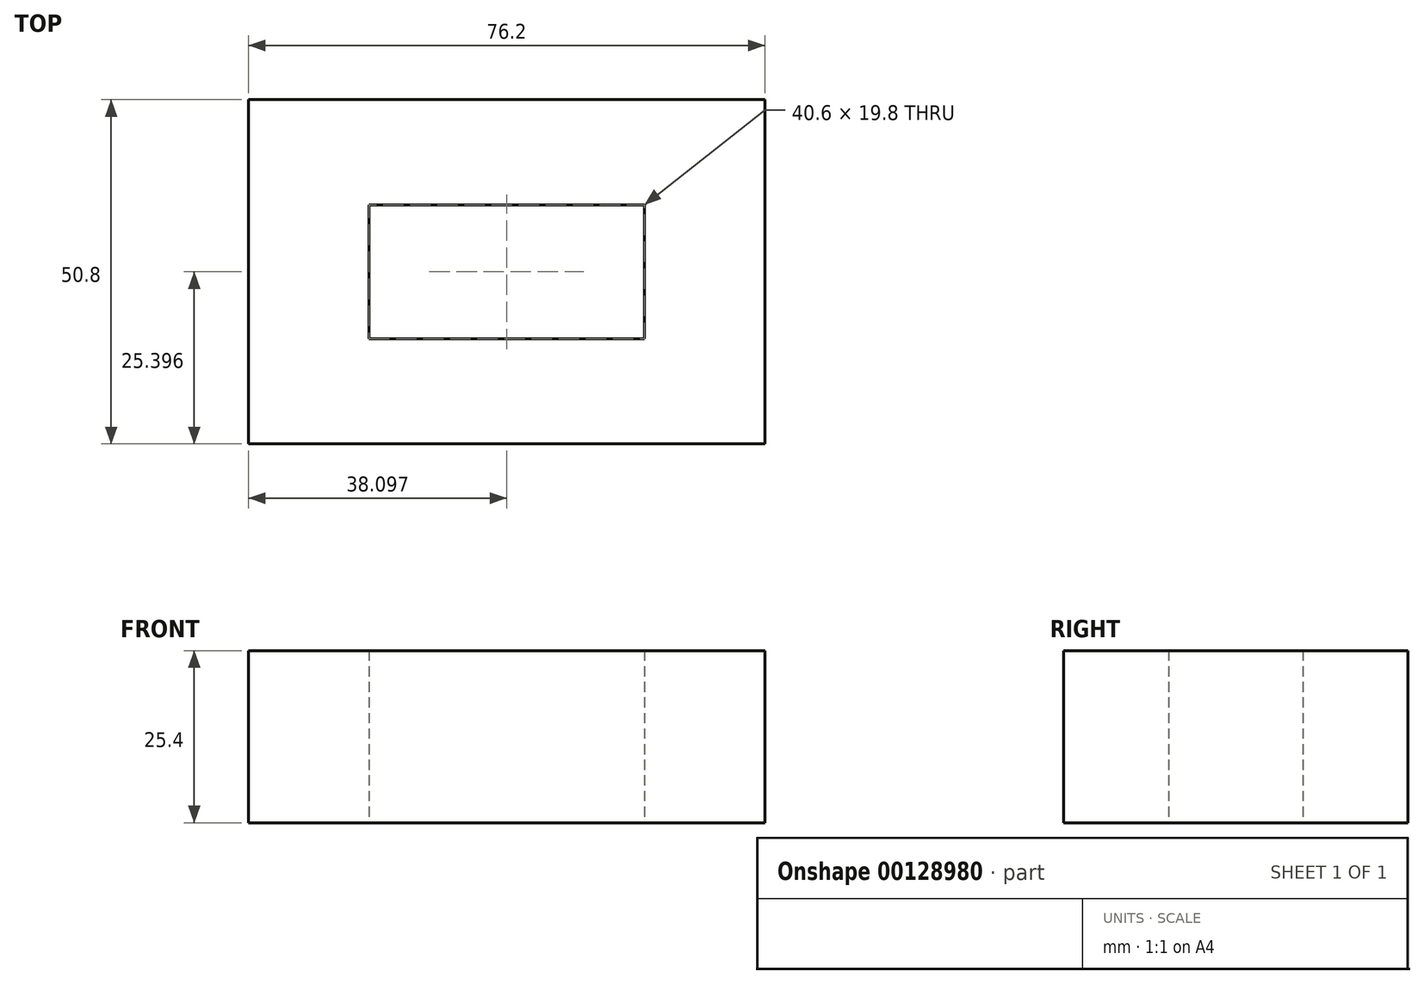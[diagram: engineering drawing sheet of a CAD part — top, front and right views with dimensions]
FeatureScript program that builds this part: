
annotation { "Feature Type Name" : "Feature", "Feature Type Description" : "" }
export const myFeature = defineFeature(function(context is Context, id is Id, definition is map)
    precondition{}
    {
        {
            var Q0;
            Q0=qCreatedBy(makeId("Top.planeOp"),FACE);
            var sketch = newSketch(context, id + "F0", { "sketchPlane" : qUnion([Q0])});
            skLineSegment(sketch, "E0.bottom", {"start": v(-33.18, 33.1) * mm, "end": v(43.02, 33.1) * mm});
            skLineSegment(sketch, "E0.top", {"start": v(-33.18, -17.7) * mm, "end": v(43.02, -17.7) * mm});
            skLineSegment(sketch, "E0.left", {"start": v(-33.18, 33.1) * mm, "end": v(-33.18, -17.7) * mm});
            skLineSegment(sketch, "E0.right", {"start": v(43.02, 33.1) * mm, "end": v(43.02, -17.7) * mm});
            skLineSegment(sketch, "E1", {"start": v(-33.18, 33.1) * mm, "end": v(43.02, -17.7) * mm, "construction": true});
            skPoint(sketch, "E2", {"position": v(4.92, 7.7) * mm});
            skLineSegment(sketch, "E3.bottom", {"start": v(-15.38, 17.6) * mm, "end": v(25.22, 17.6) * mm});
            skLineSegment(sketch, "E3.top", {"start": v(-15.38, -2.2) * mm, "end": v(25.22, -2.2) * mm});
            skLineSegment(sketch, "E3.left", {"start": v(-15.38, 17.6) * mm, "end": v(-15.38, -2.2) * mm});
            skLineSegment(sketch, "E3.right", {"start": v(25.22, 17.6) * mm, "end": v(25.22, -2.2) * mm});
            skSolve(sketch);
        }
        {
            var Q0;
            Q0=makeQuery(id+"F0.imprint","IMPRINT",FACE,{"disambiguationData":[TD([[makeQuery(id+"F0.imprint","IMPRINT",EDGE,{"derivedFrom":sQuery(id+"F0.wireOp",EDGE,"E0.bottom")}),-1.0]])]});
            extrude(context, id + "F1", {"entities" : qUnion([Q0]), "depth" : 25.4 * mm});
        }
    });
